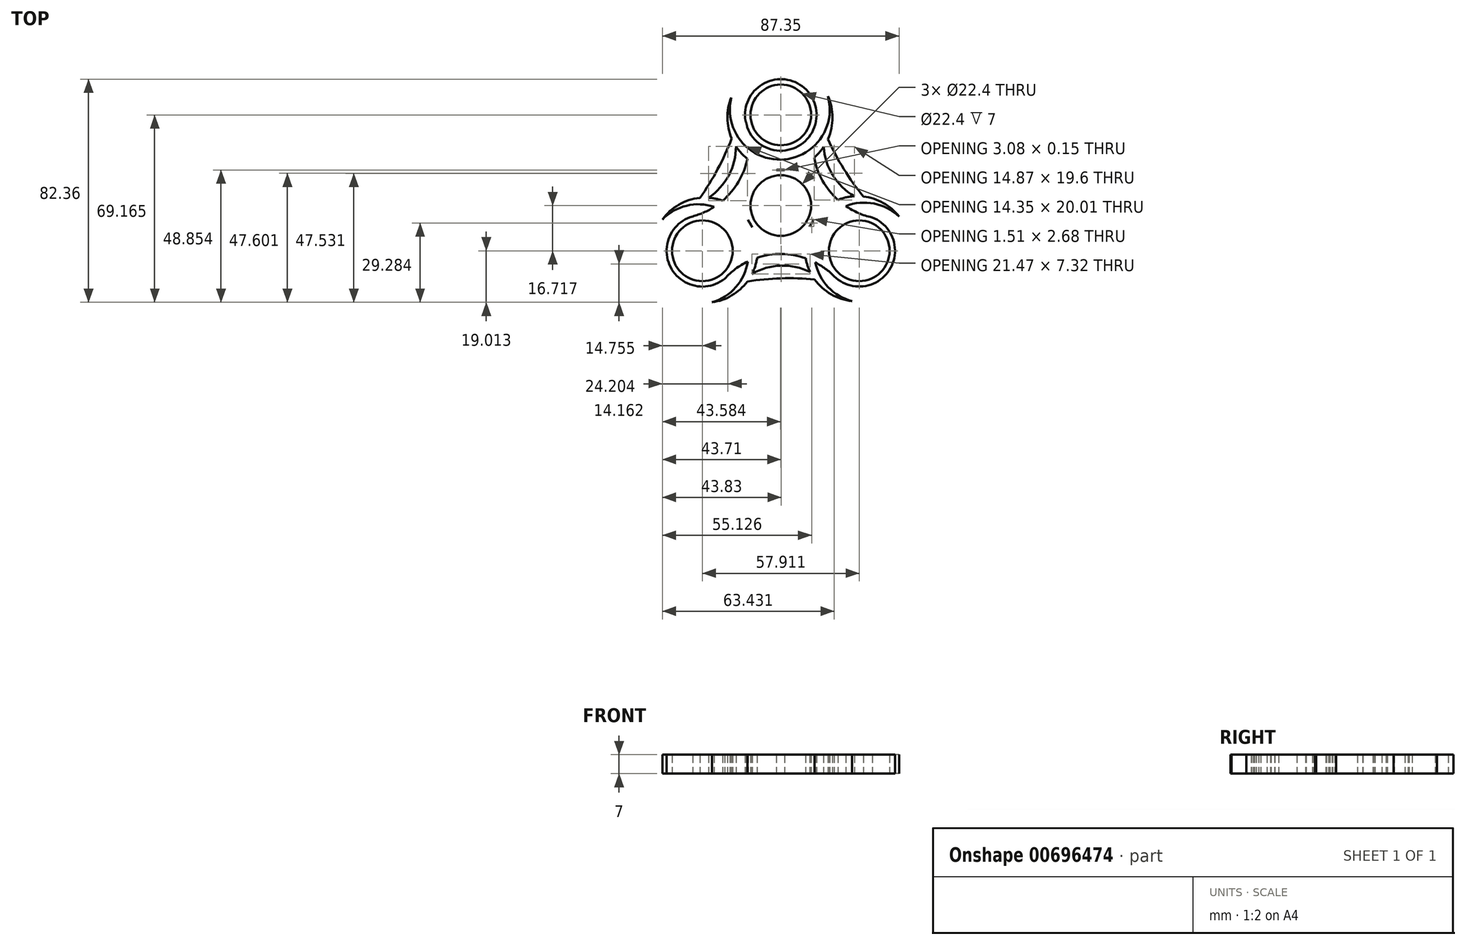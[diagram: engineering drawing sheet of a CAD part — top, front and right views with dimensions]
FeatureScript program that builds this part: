
annotation { "Feature Type Name" : "Feature", "Feature Type Description" : "" }
export const myFeature = defineFeature(function(context is Context, id is Id, definition is map)
    precondition{}
    {
        {
            var Q0;
            Q0=qCreatedBy(makeId("Top.planeOp"),FACE);
            var sketch = newSketch(context, id + "F0", { "sketchPlane" : qUnion([Q0])});
            skCircle(sketch, "E0", {"center": v(0, 0) * mm, "radius": 11.2 * mm});
            skCircle(sketch, "E1", {"center": v(0, 0) * mm, "radius": 13.2 * mm});
            skCircle(sketch, "E2", {"center": v(0, 33.43) * mm, "radius": 11.2 * mm});
            skCircle(sketch, "E3", {"center": v(0, 33.43) * mm, "radius": 13.2 * mm});
            skCircle(sketch, "E4.1.0", {"center": v(-28.96, -16.72) * mm, "radius": 11.2 * mm});
            skCircle(sketch, "E4.1.1", {"center": v(-28.96, -16.72) * mm, "radius": 13.2 * mm});
            skCircle(sketch, "E4.2.0", {"center": v(28.96, -16.72) * mm, "radius": 11.2 * mm});
            skCircle(sketch, "E4.2.1", {"center": v(28.96, -16.72) * mm, "radius": 13.2 * mm});
            skArc(sketch, "E5", {"start": v(-32.54, -4.01) * mm, "mid": v(-15.19, 9.52) * mm, "end": v(-13.05, 31.42) * mm});
            skArc(sketch, "E6.1.0", {"start": v(19.74, -26.17) * mm, "mid": v(-0.65, -17.91) * mm, "end": v(-20.69, -27) * mm});
            skArc(sketch, "E6.2.0", {"start": v(12.8, 30.18) * mm, "mid": v(15.84, 8.4) * mm, "end": v(33.74, -4.41) * mm});
            skArc(sketch, "E7", {"start": v(-18.25, 39.86) * mm, "mid": v(0, 13.05) * mm, "end": v(17.37, 40.44) * mm});
            skArc(sketch, "E8", {"start": v(-18.25, 39.86) * mm, "mid": v(-0.06, 16.93) * mm, "end": v(17.37, 40.44) * mm});
            skArc(sketch, "E9.1.0", {"start": v(-25.4, -35.73) * mm, "mid": v(-11.3, -6.52) * mm, "end": v(-43.71, -5.17) * mm});
            skArc(sketch, "E9.1.1", {"start": v(-25.4, -35.73) * mm, "mid": v(-14.63, -8.51) * mm, "end": v(-43.71, -5.17) * mm});
            skArc(sketch, "E9.2.0", {"start": v(43.64, -4.12) * mm, "mid": v(11.3, -6.53) * mm, "end": v(26.34, -35.27) * mm});
            skArc(sketch, "E9.2.1", {"start": v(43.64, -4.12) * mm, "mid": v(14.69, -8.41) * mm, "end": v(26.34, -35.27) * mm});
            skArc(sketch, "E10", {"start": v(-26.68, 2.87) * mm, "mid": v(-19.23, 11.06) * mm, "end": v(-16.54, 21.8) * mm});
            skArc(sketch, "E11", {"start": v(-29.89, 2.81) * mm, "mid": v(-23.3, 13.4) * mm, "end": v(-18.12, 24.74) * mm});
            skArc(sketch, "E12.1.0", {"start": v(12.5, -27.29) * mm, "mid": v(0.04, -26.88) * mm, "end": v(-12.37, -28.06) * mm});
            skArc(sketch, "E12.1.1", {"start": v(10.86, -24.54) * mm, "mid": v(0.03, -22.18) * mm, "end": v(-10.62, -25.23) * mm});
            skArc(sketch, "E12.2.0", {"start": v(17.38, 24.48) * mm, "mid": v(23.25, 13.48) * mm, "end": v(30.49, 3.32) * mm});
            skArc(sketch, "E12.2.1", {"start": v(15.82, 21.67) * mm, "mid": v(19.2, 11.12) * mm, "end": v(27.15, 3.42) * mm});
            skSolve(sketch);
        }
        {
            var Q0;
            {var subQ3=sQuery(id+"F0.wireOp",EDGE,"E7");var subQ5=sQuery(id+"F0.wireOp",EDGE,"E1");var subQ6=makeQuery(id+"F0.imprint","INTERSECT",VERTEX,{"disambiguationData":[OD(0.0)],"derivedFrom":[subQ5,subQ3]});Q0=makeQuery(id+"F0.imprint","IMPRINT",FACE,{"disambiguationData":[TD([[makeQuery(id+"F0.imprint","IMPRINT",EDGE,{"disambiguationData":[TD([[subQ6,1.0]])],"derivedFrom":subQ5}),-1.0]])]});}
            var Q1;
            {var subQ0=sQuery(id+"F0.wireOp",EDGE,"E8");var subQ5=sQuery(id+"F0.wireOp",EDGE,"E6.2.0");var subQ7=makeQuery(id+"F0.imprint","INTERSECT",VERTEX,{"derivedFrom":[subQ5,subQ0]});Q1=makeQuery(id+"F0.imprint","IMPRINT",FACE,{"disambiguationData":[TD([[makeQuery(id+"F0.imprint","IMPRINT",EDGE,{"disambiguationData":[TD([[subQ7,-1.0]])],"derivedFrom":subQ5}),1.0]])]});}
            var Q2;
            {var subQ2=sQuery(id+"F0.wireOp",EDGE,"E5");var subQ5=sQuery(id+"F0.wireOp",EDGE,"E8");var subQ7=makeQuery(id+"F0.imprint","INTERSECT",VERTEX,{"derivedFrom":[subQ2,subQ5]});Q2=makeQuery(id+"F0.imprint","IMPRINT",FACE,{"disambiguationData":[TD([[makeQuery(id+"F0.imprint","IMPRINT",EDGE,{"disambiguationData":[TD([[subQ7,1.0]])],"derivedFrom":subQ2}),1.0]])]});}
            var Q3;
            Q3=makeQuery(id+"F0.imprint","IMPRINT",FACE,{"disambiguationData":[TD([[makeQuery(id+"F0.imprint","IMPRINT",EDGE,{"derivedFrom":sQuery(id+"F0.wireOp",EDGE,"E2")}),-1.0]])]});
            var Q4;
            {var subQ0=sQuery(id+"F0.wireOp",EDGE,"E5");var subQ1=sQuery(id+"F0.wireOp",EDGE,"E3");var subQ2=makeQuery(id+"F0.imprint","INTERSECT",VERTEX,{"disambiguationData":[OD(1.0)],"derivedFrom":[subQ1,subQ0]});Q4=makeQuery(id+"F0.imprint","IMPRINT",FACE,{"disambiguationData":[TD([[makeQuery(id+"F0.imprint","IMPRINT",EDGE,{"disambiguationData":[TD([[subQ2,-1.0]])],"derivedFrom":subQ1}),-1.0]])]});}
            var Q5;
            Q5=makeQuery(id+"F0.imprint","IMPRINT",FACE,{"disambiguationData":[TD([[makeQuery(id+"F0.imprint","IMPRINT",EDGE,{"derivedFrom":sQuery(id+"F0.wireOp",EDGE,"E4.2.0")}),-1.0]])]});
            var Q6;
            {var subQ3=sQuery(id+"F0.wireOp",EDGE,"E9.2.0");var subQ5=sQuery(id+"F0.wireOp",EDGE,"E1");var subQ10=makeQuery(id+"F0.imprint","INTERSECT",VERTEX,{"disambiguationData":[OD(0.0)],"derivedFrom":[subQ5,subQ3]});Q6=makeQuery(id+"F0.imprint","IMPRINT",FACE,{"disambiguationData":[TD([[makeQuery(id+"F0.imprint","IMPRINT",EDGE,{"disambiguationData":[TD([[subQ10,-1.0]])],"derivedFrom":subQ5}),-1.0]])]});}
            var Q7;
            {var subQ0=sQuery(id+"F0.wireOp",EDGE,"E6.2.0");var subQ1=sQuery(id+"F0.wireOp",EDGE,"E4.2.1");var subQ2=makeQuery(id+"F0.imprint","INTERSECT",VERTEX,{"disambiguationData":[OD(1.0)],"derivedFrom":[subQ1,subQ0]});Q7=makeQuery(id+"F0.imprint","IMPRINT",FACE,{"disambiguationData":[TD([[makeQuery(id+"F0.imprint","IMPRINT",EDGE,{"disambiguationData":[TD([[subQ2,-1.0]])],"derivedFrom":subQ1}),-1.0]])]});}
            var Q8;
            {var subQ0=sQuery(id+"F0.wireOp",EDGE,"E7");var subQ1=sQuery(id+"F0.wireOp",EDGE,"E1");var subQ2=makeQuery(id+"F0.imprint","INTERSECT",VERTEX,{"disambiguationData":[OD(1.0)],"derivedFrom":[subQ1,subQ0]});Q8=makeQuery(id+"F0.imprint","IMPRINT",FACE,{"disambiguationData":[TD([[makeQuery(id+"F0.imprint","IMPRINT",EDGE,{"disambiguationData":[TD([[subQ2,1.0]])],"derivedFrom":subQ1}),-1.0]])]});}
            var Q9;
            {var subQ0=sQuery(id+"F0.wireOp",EDGE,"E9.1.0");var subQ1=sQuery(id+"F0.wireOp",EDGE,"E1");var subQ2=makeQuery(id+"F0.imprint","INTERSECT",VERTEX,{"disambiguationData":[OD(1.0)],"derivedFrom":[subQ1,subQ0]});Q9=makeQuery(id+"F0.imprint","IMPRINT",FACE,{"disambiguationData":[TD([[makeQuery(id+"F0.imprint","IMPRINT",EDGE,{"disambiguationData":[TD([[subQ2,-1.0]])],"derivedFrom":subQ1}),-1.0]])]});}
            var Q10;
            Q10=makeQuery(id+"F0.imprint","IMPRINT",FACE,{"disambiguationData":[TD([[makeQuery(id+"F0.imprint","IMPRINT",EDGE,{"derivedFrom":sQuery(id+"F0.wireOp",EDGE,"E0")}),-1.0]])]});
            var Q11;
            {var subQ3=sQuery(id+"F0.wireOp",EDGE,"E9.1.0");var subQ5=sQuery(id+"F0.wireOp",EDGE,"E1");var subQ9=makeQuery(id+"F0.imprint","INTERSECT",VERTEX,{"disambiguationData":[OD(0.0)],"derivedFrom":[subQ5,subQ3]});Q11=makeQuery(id+"F0.imprint","IMPRINT",FACE,{"disambiguationData":[TD([[makeQuery(id+"F0.imprint","IMPRINT",EDGE,{"disambiguationData":[TD([[subQ9,-1.0]])],"derivedFrom":subQ5}),-1.0]])]});}
            var Q12;
            {var subQ0=sQuery(id+"F0.wireOp",EDGE,"E10");Q12=makeQuery(id+"F0.imprint","IMPRINT",FACE,{"disambiguationData":[TD([[makeQuery(id+"F0.imprint","IMPRINT",EDGE,{"derivedFrom":subQ0}),1.0]])]});}
            var Q13;
            {var subQ0=sQuery(id+"F0.wireOp",EDGE,"E12.2.0");Q13=makeQuery(id+"F0.imprint","IMPRINT",FACE,{"disambiguationData":[TD([[makeQuery(id+"F0.imprint","IMPRINT",EDGE,{"derivedFrom":subQ0}),-1.0]])]});}
            var Q14;
            {var subQ0=sQuery(id+"F0.wireOp",EDGE,"E12.1.0");Q14=makeQuery(id+"F0.imprint","IMPRINT",FACE,{"disambiguationData":[TD([[makeQuery(id+"F0.imprint","IMPRINT",EDGE,{"derivedFrom":subQ0}),-1.0]])]});}
            var Q15;
            {var subQ0=sQuery(id+"F0.wireOp",EDGE,"E9.1.1");var subQ5=sQuery(id+"F0.wireOp",EDGE,"E5");var subQ7=makeQuery(id+"F0.imprint","INTERSECT",VERTEX,{"derivedFrom":[subQ5,subQ0]});Q15=makeQuery(id+"F0.imprint","IMPRINT",FACE,{"disambiguationData":[TD([[makeQuery(id+"F0.imprint","IMPRINT",EDGE,{"disambiguationData":[TD([[subQ7,-1.0]])],"derivedFrom":subQ5}),1.0]])]});}
            var Q16;
            {var subQ0=sQuery(id+"F0.wireOp",EDGE,"E6.1.0");var subQ1=sQuery(id+"F0.wireOp",EDGE,"E4.1.1");var subQ2=makeQuery(id+"F0.imprint","INTERSECT",VERTEX,{"disambiguationData":[OD(1.0)],"derivedFrom":[subQ1,subQ0]});Q16=makeQuery(id+"F0.imprint","IMPRINT",FACE,{"disambiguationData":[TD([[makeQuery(id+"F0.imprint","IMPRINT",EDGE,{"disambiguationData":[TD([[subQ2,-1.0]])],"derivedFrom":subQ1}),-1.0]])]});}
            var Q17;
            {var subQ2=sQuery(id+"F0.wireOp",EDGE,"E6.1.0");var subQ5=sQuery(id+"F0.wireOp",EDGE,"E9.1.1");var subQ7=makeQuery(id+"F0.imprint","INTERSECT",VERTEX,{"derivedFrom":[subQ2,subQ5]});Q17=makeQuery(id+"F0.imprint","IMPRINT",FACE,{"disambiguationData":[TD([[makeQuery(id+"F0.imprint","IMPRINT",EDGE,{"disambiguationData":[TD([[subQ7,1.0]])],"derivedFrom":subQ2}),1.0]])]});}
            var Q18;
            {var subQ0=sQuery(id+"F0.wireOp",EDGE,"E9.2.1");var subQ4=sQuery(id+"F0.wireOp",EDGE,"E6.1.0");var subQ5=makeQuery(id+"F0.imprint","INTERSECT",VERTEX,{"derivedFrom":[subQ4,subQ0]});Q18=makeQuery(id+"F0.imprint","IMPRINT",FACE,{"disambiguationData":[TD([[makeQuery(id+"F0.imprint","IMPRINT",EDGE,{"disambiguationData":[TD([[subQ5,-1.0]])],"derivedFrom":subQ4}),1.0]])]});}
            var Q19;
            {var subQ2=sQuery(id+"F0.wireOp",EDGE,"E6.2.0");var subQ5=sQuery(id+"F0.wireOp",EDGE,"E9.2.1");var subQ7=makeQuery(id+"F0.imprint","INTERSECT",VERTEX,{"derivedFrom":[subQ2,subQ5]});Q19=makeQuery(id+"F0.imprint","IMPRINT",FACE,{"disambiguationData":[TD([[makeQuery(id+"F0.imprint","IMPRINT",EDGE,{"disambiguationData":[TD([[subQ7,1.0]])],"derivedFrom":subQ2}),1.0]])]});}
            var Q20;
            {var subQ0=sQuery(id+"F0.wireOp",EDGE,"E7");var subQ1=sQuery(id+"F0.wireOp",EDGE,"E1");var subQ2=makeQuery(id+"F0.imprint","INTERSECT",VERTEX,{"disambiguationData":[OD(0.0)],"derivedFrom":[subQ1,subQ0]});Q20=makeQuery(id+"F0.imprint","IMPRINT",FACE,{"disambiguationData":[TD([[makeQuery(id+"F0.imprint","IMPRINT",EDGE,{"disambiguationData":[TD([[subQ2,-1.0]])],"derivedFrom":subQ1}),-1.0]])]});}
            var Q21;
            Q21=makeQuery(id+"F0.imprint","IMPRINT",FACE,{"disambiguationData":[TD([[makeQuery(id+"F0.imprint","IMPRINT",EDGE,{"derivedFrom":sQuery(id+"F0.wireOp",EDGE,"E4.1.0")}),-1.0]])]});
            extrude(context, id + "F1", {"entities" : qUnion([Q0, Q1, Q2, Q3, Q4, Q5, Q6, Q7, Q8, Q9, Q10, Q11, Q12, Q13, Q14, Q15, Q16, Q17, Q18, Q19, Q20, Q21]), "depth" : 7 * mm, "offsetDistance" : 25 * mm});
        }
    });
